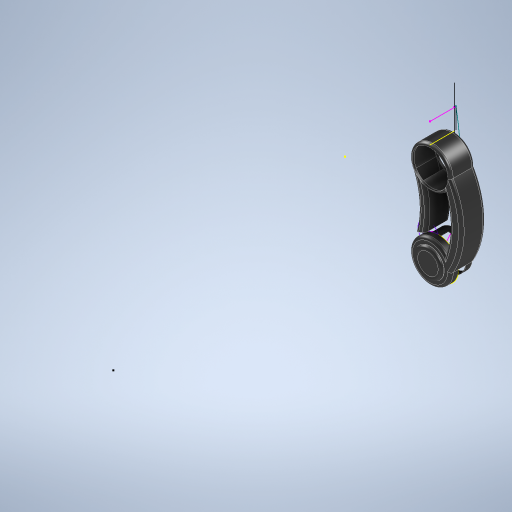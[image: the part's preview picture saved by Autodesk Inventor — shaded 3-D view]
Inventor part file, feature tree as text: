
AUTODESK INVENTOR PART (.ipt)
format: ipt  version: 2024 (Build 280153000, 153)  size: 484,864 bytes
history: native  units: mm
features: extrude x7, sketch x6, fillet x4, shell x1
ambient origin geometry x8: Origin, YZ Plane, XZ Plane, XY Plane, X Axis, Y Axis, Z Axis, Center Point
bodies: Solid1 (feature_tree)
feature tree (18):
  sketch  "Sketch1"  dims[d0=100.0mm d1=88.0mm]
  extrude  "Extrusion1"  Depth=88.0mm
  extrude  "Extrusion2"  Depth=20.0mm TaperAngle=0.0deg
  extrude  "Extrusion3"  Depth=100.0mm
  extrude  "Extrusion4"  Depth=50.0mm TaperAngle=0.0deg
  shell  "Shell1"  Thickness=100.0mm
  sketch  "Sketch5"  dims[d8=25.0mm d9=50.0mm d10=0.0mm d13=100.0mm]
  extrude  "Extrusion6"  Depth=60.0mm TaperAngle=0.0deg
  extrude  "Extrusion7"  Depth=7.0mm
  extrude  "Extrusion8"  Depth=50.0mm
  fillet  "Fillet1"  Radius=10.0mm
  sketch  "Sketch6"  dims[d14=88.0mm d15=60.0mm d16=0.0mm]
  fillet  "Fillet2"  Radius=5.0mm
  fillet  "Fillet3"  Radius=5.0mm
  fillet  "Fillet4"  Radius=6.0mm
  sketch  "Sketch7"  dims[d19=5.0mm d20=70.0mm d21=50.0mm d22=10.0mm d23=0.0mm d24=5.0mm d25=0.0mm d26=5.0mm d27=0.0mm d28=6.0mm d31=200.0mm d32=0.0mm d33=200.0mm d34=200.0mm d35=200.0mm d36=200.0mm d37=7.0mm d38=7.0mm d39=7.0mm d40=0.5mm d41=0.872665mm d42=0.5mm d43=0.872665mm]
  sketch  "Sketch2"  dims[d2=85.0mm d3=20.0mm d4=0.0mm]
  sketch  "Sketch3"  dims[d5=40.0mm d6=0.0mm d7=100.0mm]
